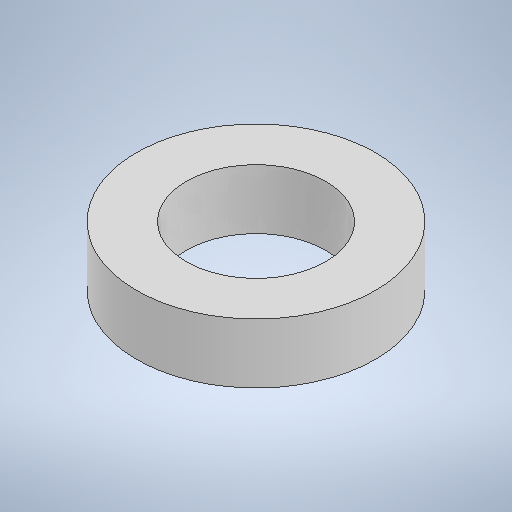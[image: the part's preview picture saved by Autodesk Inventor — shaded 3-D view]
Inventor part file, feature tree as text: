
AUTODESK INVENTOR PART (.ipt)
format: ipt  version: 2025.1 (Build 291241000, 241)  size: 259,072 bytes
history: native  units: mm
features: extrude x1, sketch x1
ambient origin geometry x8: Origin, YZ Plane, XZ Plane, XY Plane, X Axis, Y Axis, Z Axis, Center Point
bodies: Solid1 (feature_tree)
feature tree (2):
  extrude  "Extrusion1"  Depth=3.0mm
  sketch  "Sketch1"  dims[d0=12.0mm d1=7.0mm d2=3.0mm d3=0.0mm]
